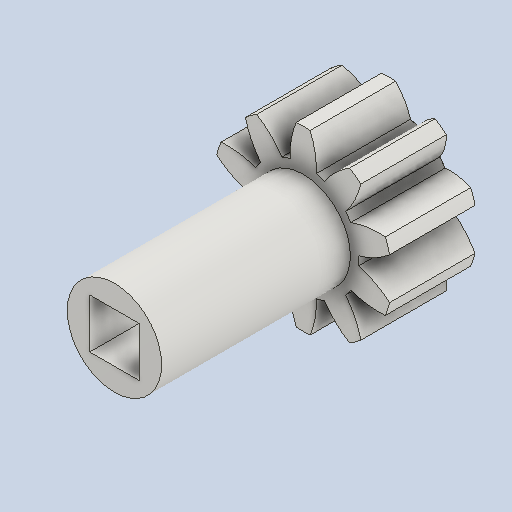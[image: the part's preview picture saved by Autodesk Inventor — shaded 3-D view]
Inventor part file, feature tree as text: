
AUTODESK INVENTOR PART (.ipt)
format: ipt  version: 2022 (Build 260153000, 153)  size: 262,144 bytes
history: native  units: in
note: dims shown in document units (in); Inventor stores cm internally (conversion verified against a paired STEP export)
features: other x12, sketch x6, plane x3
ambient origin geometry x8: Origin, YZ Plane, XZ Plane, XY Plane, X Axis, Y Axis, Z Axis, Center Point
bodies: Solid1 (feature_tree)
feature tree (21):
  other  "Spur Gear1"
  other  "Solid1::Spur Gear1"
  other  "TaggingFeature1"
  sketch  "Sketch1"  dims[d0=0.3937in]
  sketch  "Sketch2"  dims[d9=0.0in d14=0.0in d15=0.9352in d16=0.0in d17=0.0in d18=0.0in d19=0.9352in]
  sketch  "Sketch3"
  sketch  "Sketch4"
  sketch  "Sketch5"
  sketch  "Sketch6"
  plane  "XZ Plane_1"
  plane  "Work Plane2"
  plane  "Work Plane3"
  other  "Srf1"
  other  "Srf1::Derived"
  other  "Start plane iMate"
  other  "Distance iMate"
  other  "Position iMate"
  other  "Mesh iMate"
  other  "Axis iMate"
  other  "Mesh iMate2"
  other  "Align iMate"
